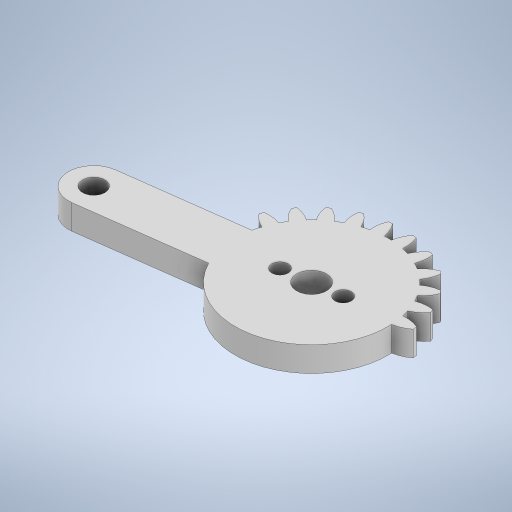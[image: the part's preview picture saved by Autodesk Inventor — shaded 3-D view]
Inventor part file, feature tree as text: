
AUTODESK INVENTOR PART (.ipt)
format: ipt  version: 2024.1 (Build 281209000, 209)  size: 348,160 bytes
history: native  units: in
note: dims shown in document units (in); Inventor stores cm internally (conversion verified against a paired STEP export)
features: extrude x1, direct_edit x1, sketch x1, other x1
ambient origin geometry x8: Origin, YZ Plane, XZ Plane, XY Plane, X Axis, Y Axis, Z Axis, Center Point
bodies: Solid1 (feature_tree)
feature tree (4):
  extrude  "Extrusion1"  Depth=0.3937in
  direct_edit  "Direct Edit1"
  sketch  "Sketch1"  dims[d1=3.5433in d2=24.2126in d3=4.7244in d6=4.4488in d7=2.5984in d8=4.4488in d9=2.5984in d10=4.3307in d12=150.0deg d14=3.937in d15=0.0in d16=0.0394in d17=0.3937in d18=0.3937in]
  other  "Scale1"
